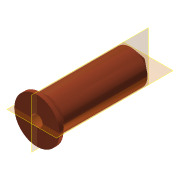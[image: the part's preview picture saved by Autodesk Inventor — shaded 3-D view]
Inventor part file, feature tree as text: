
AUTODESK INVENTOR PART (.ipt)
format: ipt  version: 2014 (Build 180170000, 170)  size: 156,672 bytes
history: native  units: mm
features: sketch x5, extrude x3, revolve x2, chamfer x1
ambient origin geometry x8: Origin, YZ Plane, XZ Plane, XY Plane, X Axis, Y Axis, Z Axis, Center Point
bodies: Solid1 (feature_tree)
feature tree (11):
  extrude  "Extrusion1"  Depth=1.0mm TaperAngle=0.0deg
  extrude  "Extrusion2"  Depth=15.584mm TaperAngle=0.0deg
  extrude  "Extrusion3"  Depth=21.0mm TaperAngle=0.0deg
  revolve  "Revolution1"  [1 undecoded]
  revolve  "Revolution2"  Angle=90.0deg
  chamfer  "Chamfer1"  Distance=0.7mm
  sketch  "Sketch1"  dims[d0=8.0mm d1=1.0mm d2=0.0mm]
  sketch  "Sketch2"  dims[d3=6.0mm d4=15.584mm d5=0.0mm]
  sketch  "Sketch3"  dims[d6=2.0mm d7=21.0mm d8=0.0mm]
  sketch  "Sketch4"  dims[d9=6.981317mm d10=0.2mm]
  sketch  "Sketch5"  dims[d11=30.0deg d13=90.0deg d14=0.7mm d15=90.0deg d16=0.3mm d17=2.0mm d18=45.0deg d19=45.0deg d20=0.05mm d21=0.3mm d22=0.05mm]
note: 1 required parameter value undecoded (feature->parameter linkage not recoverable at this tier; creation-order binding heuristic only, values carry confidence <= 0.55)
